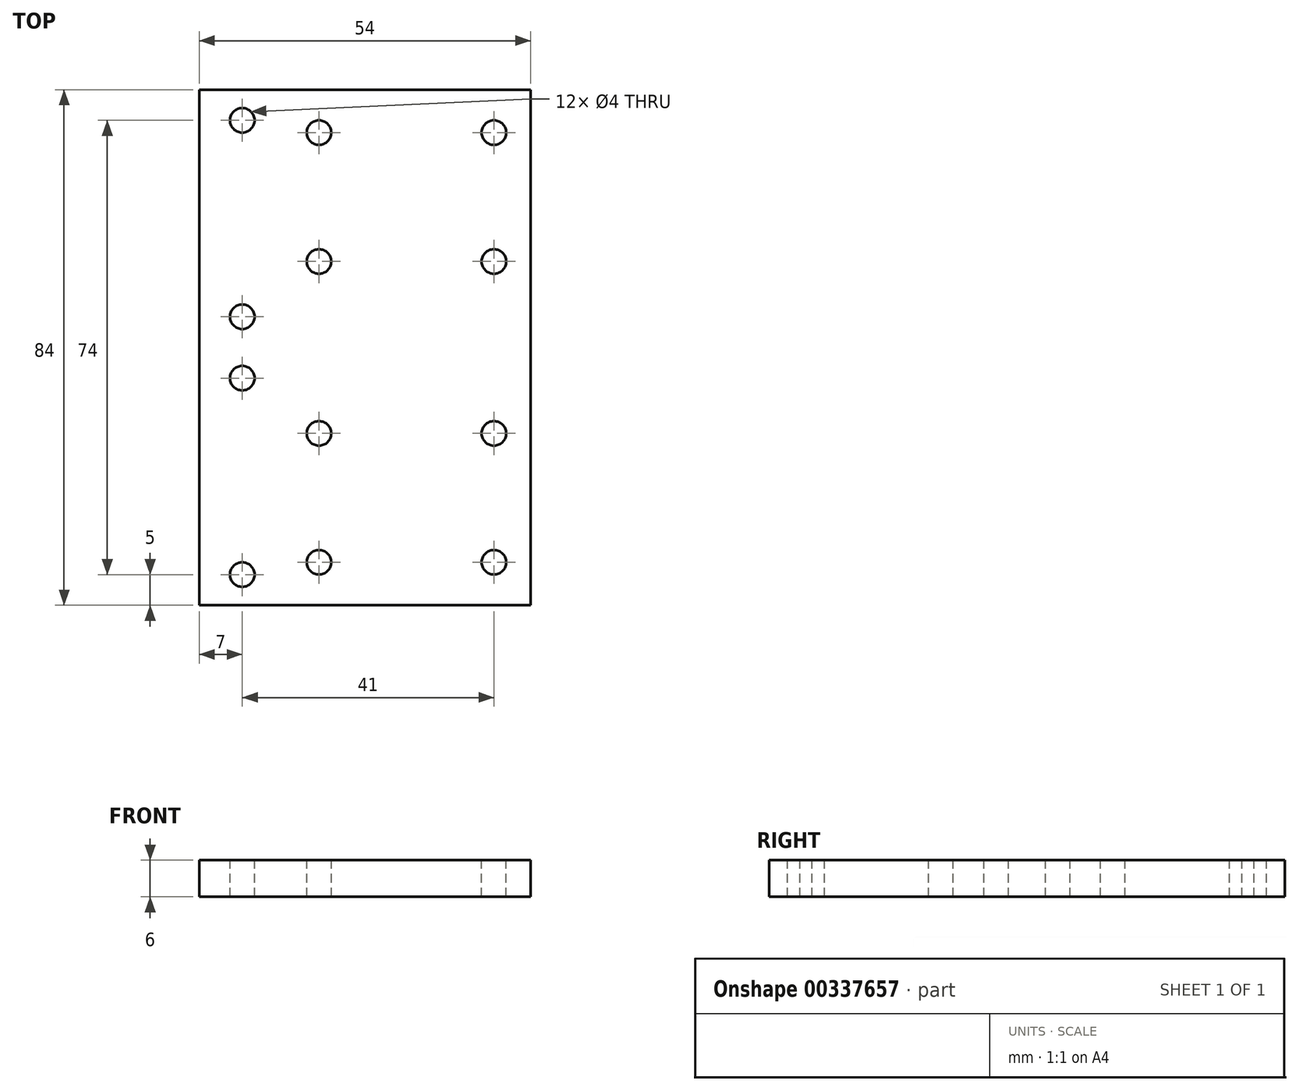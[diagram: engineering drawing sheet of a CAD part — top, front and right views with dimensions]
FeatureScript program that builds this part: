
annotation { "Feature Type Name" : "Feature", "Feature Type Description" : "" }
export const myFeature = defineFeature(function(context is Context, id is Id, definition is map)
    precondition{}
    {
        {
            var Q0;
            Q0=qCreatedBy(makeId("Top.planeOp"),FACE);
            var sketch = newSketch(context, id + "F0", { "sketchPlane" : qUnion([Q0])});
            skLineSegment(sketch, "E0.bottom", {"start": v(27, -42) * mm, "end": v(-27, -42) * mm});
            skLineSegment(sketch, "E0.top", {"start": v(27, 42) * mm, "end": v(-27, 42) * mm});
            skLineSegment(sketch, "E0.left", {"start": v(27, -42) * mm, "end": v(27, 42) * mm});
            skLineSegment(sketch, "E0.right", {"start": v(-27, -42) * mm, "end": v(-27, 42) * mm});
            skPoint(sketch, "E0.middle", {"position": v(0, 0) * mm});
            skSolve(sketch);
        }
        {
            var Q0;
            Q0 = qSketchRegion(id + "F0", true);
            extrude(context, id + "F1", {"entities" : qUnion([Q0]), "depth" : 6 * mm});
        }
        {
            var Q0;
            Q0=makeQuery(id+"F1.opExtrude","CAP_FACE",FACE,{"disambiguationData":[OSD([sQuery(id+"F0.wireOp",EDGE,"E0.bottom"),sQuery(id+"F0.wireOp",EDGE,"E0.top"),sQuery(id+"F0.wireOp",EDGE,"E0.left"),sQuery(id+"F0.wireOp",EDGE,"E0.right")])],"isStart":false});
            var sketch = newSketch(context, id + "F2", { "sketchPlane" : qUnion([Q0])});
            skLineSegment(sketch, "E1", {"start": v(27, 0) * mm, "end": v(-27, 0) * mm, "construction": true});
            skLineSegment(sketch, "E2", {"start": v(-27, 0) * mm, "end": v(-27, 0) * mm});
            skLineSegment(sketch, "E3", {"start": v(0, 42) * mm, "end": v(0, -42) * mm, "construction": true});
            skLineSegment(sketch, "E4", {"start": v(0, -42) * mm, "end": v(0, -42) * mm});
            skSolve(sketch);
        }
        {
            var Q0;
            Q0=makeQuery(id+"F2.imprint","IMPRINT",FACE,{"disambiguationData":[TD([[makeQuery(id+"F2.imprint","IMPRINT",EDGE,{"derivedFrom":makeQuery(id+"F1.opExtrude","CAP_EDGE",EDGE,{"disambiguationData":[OSD([sQuery(id+"F0.wireOp",EDGE,"E0.bottom")])],"isStart":false})}),-1.0]])]});
            var sketch = newSketch(context, id + "F3", { "sketchPlane" : qUnion([Q0])});
            skPoint(sketch, "E5", {"position": v(-20, -37) * mm});
            skPoint(sketch, "E6", {"position": v(-20, 37) * mm});
            skPoint(sketch, "E7", {"position": v(21, 35) * mm});
            skPoint(sketch, "E8", {"position": v(21, -35) * mm});
            skCircle(sketch, "E9", {"center": v(-20, 37) * mm, "radius": 2 * mm});
            skCircle(sketch, "E10", {"center": v(-20, -37) * mm, "radius": 2 * mm});
            skCircle(sketch, "E11", {"center": v(21, -35) * mm, "radius": 2 * mm});
            skCircle(sketch, "E12", {"center": v(21, 35) * mm, "radius": 2 * mm});
            skLineSegment(sketch, "E13", {"start": v(21, 0) * mm, "end": v(21, 14) * mm, "construction": true});
            skLineSegment(sketch, "E14", {"start": v(21, 0) * mm, "end": v(21, -14) * mm, "construction": true});
            skCircle(sketch, "E15", {"center": v(21, 14) * mm, "radius": 2 * mm});
            skCircle(sketch, "E16", {"center": v(21, -14) * mm, "radius": 2 * mm});
            skCircle(sketch, "E17", {"center": v(-20, 5) * mm, "radius": 2 * mm});
            skCircle(sketch, "E18", {"center": v(-20, -5) * mm, "radius": 2 * mm});
            skCircle(sketch, "E19", {"center": v(-7.5, -14) * mm, "radius": 2 * mm});
            skCircle(sketch, "E20", {"center": v(-7.5, 14) * mm, "radius": 2 * mm});
            skCircle(sketch, "E21", {"center": v(-7.5, -35) * mm, "radius": 2 * mm});
            skCircle(sketch, "E22", {"center": v(-7.5, 35) * mm, "radius": 2 * mm});
            skSolve(sketch);
        }
        {
            var Q0;
            Q0=makeQuery(id+"F3.imprint","IMPRINT",FACE,{"disambiguationData":[TD([[makeQuery(id+"F3.imprint","IMPRINT",EDGE,{"derivedFrom":sQuery(id+"F3.wireOp",EDGE,"E20")}),1.0]])]});
            var Q1;
            Q1=makeQuery(id+"F3.imprint","IMPRINT",FACE,{"disambiguationData":[TD([[makeQuery(id+"F3.imprint","IMPRINT",EDGE,{"derivedFrom":sQuery(id+"F3.wireOp",EDGE,"E19")}),1.0]])]});
            var Q2;
            Q2=makeQuery(id+"F3.imprint","IMPRINT",FACE,{"disambiguationData":[TD([[makeQuery(id+"F3.imprint","IMPRINT",EDGE,{"derivedFrom":sQuery(id+"F3.wireOp",EDGE,"E17")}),1.0]])]});
            var Q3;
            Q3=makeQuery(id+"F3.imprint","IMPRINT",FACE,{"disambiguationData":[TD([[makeQuery(id+"F3.imprint","IMPRINT",EDGE,{"derivedFrom":sQuery(id+"F3.wireOp",EDGE,"E18")}),1.0]])]});
            var Q4;
            Q4=makeQuery(id+"F3.imprint","IMPRINT",FACE,{"disambiguationData":[TD([[makeQuery(id+"F3.imprint","IMPRINT",EDGE,{"derivedFrom":sQuery(id+"F3.wireOp",EDGE,"E15")}),1.0]])]});
            var Q5;
            Q5=makeQuery(id+"F3.imprint","IMPRINT",FACE,{"disambiguationData":[TD([[makeQuery(id+"F3.imprint","IMPRINT",EDGE,{"derivedFrom":sQuery(id+"F3.wireOp",EDGE,"E16")}),1.0]])]});
            var Q6;
            Q6=makeQuery(id+"F3.imprint","IMPRINT",FACE,{"disambiguationData":[TD([[makeQuery(id+"F3.imprint","IMPRINT",EDGE,{"derivedFrom":sQuery(id+"F3.wireOp",EDGE,"E11")}),1.0]])]});
            var Q7;
            Q7=makeQuery(id+"F3.imprint","IMPRINT",FACE,{"disambiguationData":[TD([[makeQuery(id+"F3.imprint","IMPRINT",EDGE,{"derivedFrom":sQuery(id+"F3.wireOp",EDGE,"E12")}),1.0]])]});
            var Q8;
            Q8=makeQuery(id+"F3.imprint","IMPRINT",FACE,{"disambiguationData":[TD([[makeQuery(id+"F3.imprint","IMPRINT",EDGE,{"derivedFrom":sQuery(id+"F3.wireOp",EDGE,"E9")}),1.0]])]});
            var Q9;
            Q9=makeQuery(id+"F3.imprint","IMPRINT",FACE,{"disambiguationData":[TD([[makeQuery(id+"F3.imprint","IMPRINT",EDGE,{"derivedFrom":sQuery(id+"F3.wireOp",EDGE,"E22")}),1.0]])]});
            var Q10;
            Q10=makeQuery(id+"F3.imprint","IMPRINT",FACE,{"disambiguationData":[TD([[makeQuery(id+"F3.imprint","IMPRINT",EDGE,{"derivedFrom":sQuery(id+"F3.wireOp",EDGE,"E10")}),1.0]])]});
            var Q11;
            Q11=makeQuery(id+"F3.imprint","IMPRINT",FACE,{"disambiguationData":[TD([[makeQuery(id+"F3.imprint","IMPRINT",EDGE,{"derivedFrom":sQuery(id+"F3.wireOp",EDGE,"E21")}),1.0]])]});
            extrude(context, id + "F4", {"entities" : qUnion([Q0, Q1, Q2, Q3, Q4, Q5, Q6, Q7, Q8, Q9, Q10, Q11]), "operationType" : NewBodyOperationType.REMOVE, "endBound" : BoundingType.UP_TO_NEXT, "oppositeDirection" : true, "depth" : 25 * mm});
        }
    });
